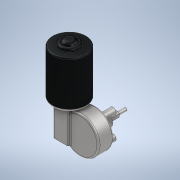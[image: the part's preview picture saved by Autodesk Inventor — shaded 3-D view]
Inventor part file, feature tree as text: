
AUTODESK INVENTOR PART (.ipt)
format: ipt  version: 2021 (Build 250183000, 183)  size: 448,000 bytes
history: native  units: mm
features: extrude x15, sketch x14, fillet x7
ambient origin geometry x8: Origin, YZ Plane, XZ Plane, XY Plane, X Axis, Y Axis, Z Axis, Center Point
bodies: Solid1 (feature_tree)
feature tree (36):
  extrude  "Extrusion1"  Depth=87.0mm TaperAngle=0.0deg
  sketch  "Sketch2"  dims[d3=36.5mm d4=33.0mm]
  sketch  "Sketch3"  dims[d11=30.0mm d13=360.0deg d15=50.0mm]
  extrude  "Extrusion2"  Depth=33.0mm
  extrude  "Extrusion3"  Depth=50.0mm
  sketch  "Sketch4"  dims[d16=87.0mm d17=0.0mm d18=15.0mm d19=0.0mm]
  extrude  "Extrusion4"  Depth=15.0mm TaperAngle=0.0deg
  extrude  "Extrusion5"  Depth=12.0mm
  sketch  "Sketch6"  dims[d23=12.0mm d24=12.0mm]
  extrude  "Extrusion6"  Depth=12.0mm
  extrude  "Extrusion7"  Depth=10.0mm
  extrude  "Extrusion8"  Depth=3.0mm
  extrude  "Extrusion9"  Depth=5.0mm TaperAngle=0.0deg
  extrude  "Extrusion10"  Depth=21.5mm TaperAngle=0.0deg
  fillet  "Fillet1"  Radius=5.0mm
  fillet  "Fillet2"  Radius=5.0mm
  fillet  "Fillet3"  Radius=3.0mm
  fillet  "Fillet4"  Radius=7.0mm
  extrude  "Extrusion11"  Depth=2.0mm
  extrude  "Extrusion12"  Depth=22.0mm
  extrude  "Extrusion13"  Depth=19.0mm TaperAngle=0.0deg
  fillet  "Fillet5"  Radius=4.0mm
  extrude  "Extrusion14"  Depth=15.5mm TaperAngle=0.0deg
  extrude  "Extrusion15"  Depth=6.0mm
  fillet  "Fillet6"  Radius=15.5mm
  fillet  "Fillet7"  Radius=5.0mm
  sketch  "Sketch1"  dims[d0=62.0mm d1=87.0mm d2=0.0mm]
  sketch  "Sketch5"  dims[d20=30.0mm d21=0.0mm d22=12.0mm]
  sketch  "Sketch7"  dims[d25=20.5mm d26=0.0mm d27=10.0mm]
  sketch  "Sketch8"  dims[d28=10.0mm d29=3.0mm]
  sketch  "Sketch9"  dims[d30=5.0mm d32=5.0mm d33=0.0mm]
  sketch  "Sketch10"  dims[d34=60.0mm d35=0.0mm d37=21.5mm d38=0.0mm d39=5.0mm d40=0.0mm d41=5.0mm d42=0.0mm d43=3.0mm d44=7.0mm]
  sketch  "Sketch11"  dims[d45=2.0mm d46=2.0mm]
  sketch  "Sketch12"  dims[d47=2.0mm d48=22.0mm]
  sketch  "Sketch13"  dims[d49=10.0mm d50=19.0mm d51=0.0mm d52=4.0mm]
  sketch  "Sketch14"  dims[d53=8.0mm d54=15.5mm d55=0.0mm d56=6.0mm d57=15.5mm d58=0.0mm d59=5.0mm d60=50.0mm d61=48.0mm d62=4.0mm d65=4.0mm d66=30.0mm d68=360.0deg d70=3.0mm d71=0.0mm d72=1.0mm d73=1.0mm d74=1.0mm d75=1.0mm d76=1.0mm d77=1.0mm d78=12.0mm d79=0.0mm d80=3.0mm d81=3.0mm]
